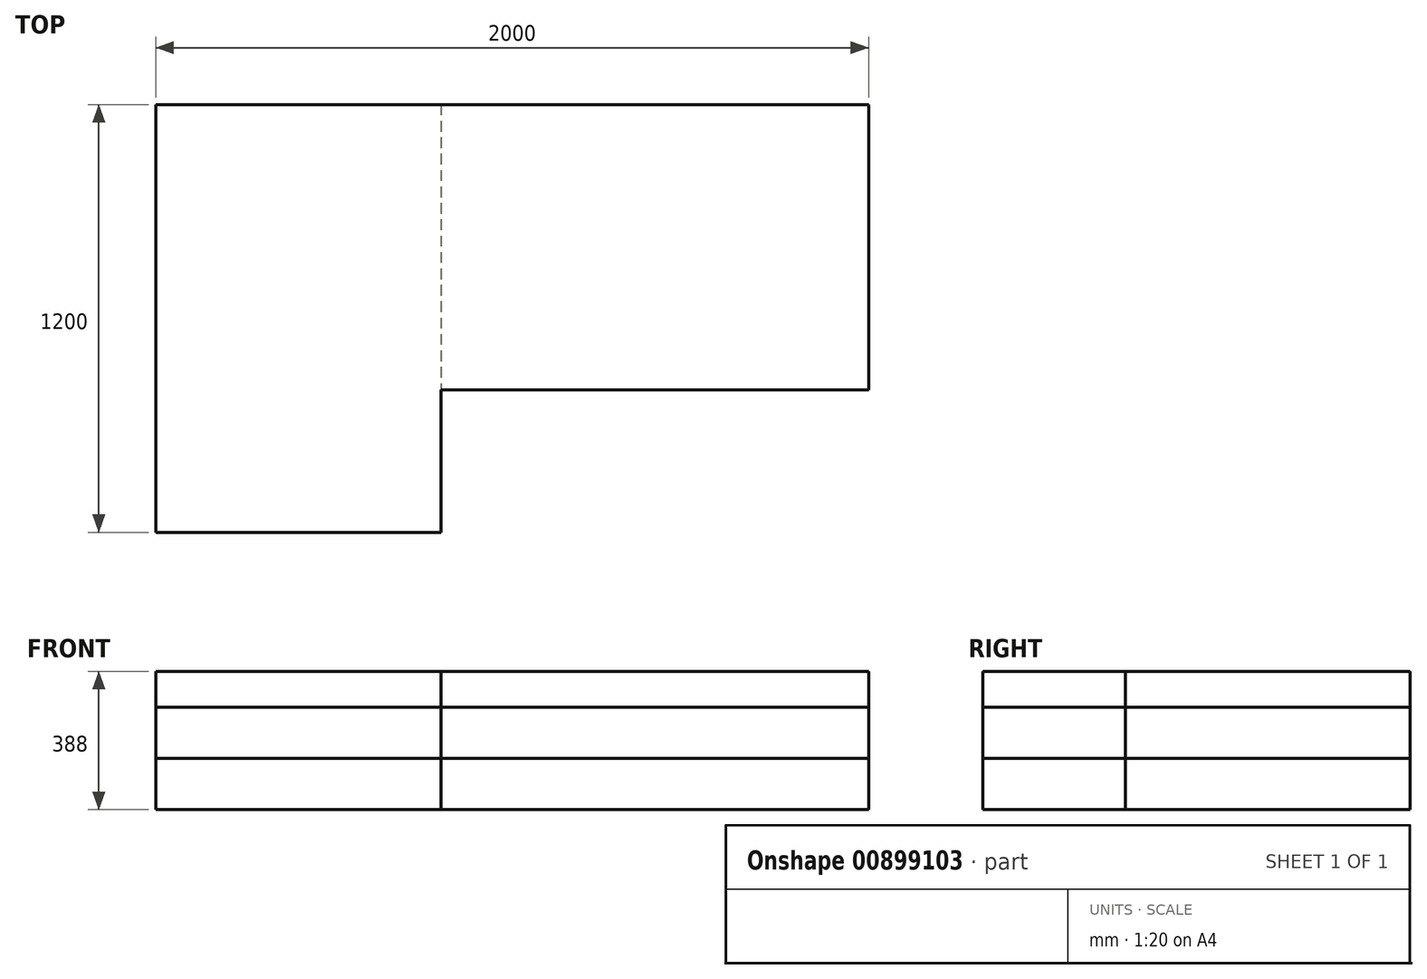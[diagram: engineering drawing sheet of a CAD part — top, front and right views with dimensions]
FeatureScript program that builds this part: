
annotation { "Feature Type Name" : "Feature", "Feature Type Description" : "" }
export const myFeature = defineFeature(function(context is Context, id is Id, definition is map)
    precondition{}
    {
        {
            var Q0;
            Q0=qCreatedBy(makeId("Top.planeOp"),FACE);
            var sketch = newSketch(context, id + "F0", { "sketchPlane" : qUnion([Q0])});
            skLineSegment(sketch, "E0.bottom", {"start": v(-200, 600) * mm, "end": v(1000, 600) * mm});
            skLineSegment(sketch, "E0.top", {"start": v(-200, -200) * mm, "end": v(1000, -200) * mm});
            skLineSegment(sketch, "E0.left", {"start": v(-200, 600) * mm, "end": v(-200, -200) * mm});
            skLineSegment(sketch, "E0.right", {"start": v(1000, 600) * mm, "end": v(1000, -200) * mm});
            skLineSegment(sketch, "E1.bottom", {"start": v(-1000, 600) * mm, "end": v(-200, 600) * mm});
            skLineSegment(sketch, "E1.top", {"start": v(-1000, -600) * mm, "end": v(-200, -600) * mm});
            skLineSegment(sketch, "E1.left", {"start": v(-1000, 600) * mm, "end": v(-1000, -600) * mm});
            skLineSegment(sketch, "E1.right", {"start": v(-200, 600) * mm, "end": v(-200, -600) * mm});
            skLineSegment(sketch, "E2", {"start": v(-1000, -600) * mm, "end": v(1000, 600) * mm, "construction": true});
            skPoint(sketch, "E3", {"position": v(0, 0) * mm});
            skSolve(sketch);
        }
        {
            var Q0;
            {var subQ1=sQuery(id+"F0.wireOp",EDGE,"E1.bottom");Q0=makeQuery(id+"F0.imprint","IMPRINT",FACE,{"disambiguationData":[TD([[makeQuery(id+"F0.imprint","IMPRINT",EDGE,{"derivedFrom":subQ1}),-1.0]])]});}
            extrude(context, id + "F1", {"entities" : qUnion([Q0]), "depth" : 144 * mm, "offsetDistance" : 25 * mm});
        }
        {
            var Q0;
            {var subQ0=sQuery(id+"F0.wireOp",EDGE,"E0.bottom");Q0=makeQuery(id+"F0.imprint","IMPRINT",FACE,{"disambiguationData":[TD([[makeQuery(id+"F0.imprint","IMPRINT",EDGE,{"derivedFrom":subQ0}),-1.0]])]});}
            extrude(context, id + "F2", {"entities" : qUnion([Q0]), "depth" : 144 * mm, "offsetDistance" : 25 * mm});
        }
        {
            var Q0;
            Q0=makeQuery(id+"F1.opExtrude","CAP_FACE",FACE,{"disambiguationData":[OSD([sQuery(id+"F0.wireOp",EDGE,"E1.bottom"),sQuery(id+"F0.wireOp",EDGE,"E1.top"),sQuery(id+"F0.wireOp",EDGE,"E1.left"),sQuery(id+"F0.wireOp",EDGE,"E1.right")])],"isStart":false});
            var sketch = newSketch(context, id + "F3", { "sketchPlane" : qUnion([Q0])});
            skLineSegment(sketch, "E4.0", {"start": v(-1000, 600) * mm, "end": v(-1000, -600) * mm});
            skLineSegment(sketch, "E5.0", {"start": v(-1000, -600) * mm, "end": v(-200, -600) * mm});
            skLineSegment(sketch, "E6.0", {"start": v(-200, 600) * mm, "end": v(-200, -600) * mm});
            skLineSegment(sketch, "E7.0", {"start": v(-1000, 600) * mm, "end": v(-200, 600) * mm});
            skLineSegment(sketch, "E8.0.0", {"start": v(1000, 600) * mm, "end": v(-200, 600) * mm});
            skLineSegment(sketch, "E8.0.1", {"start": v(-200, 600) * mm, "end": v(-200, -200) * mm});
            skLineSegment(sketch, "E8.0.2", {"start": v(-200, -200) * mm, "end": v(1000, -200) * mm});
            skLineSegment(sketch, "E8.0.3", {"start": v(1000, -200) * mm, "end": v(1000, 600) * mm});
            skSolve(sketch);
        }
        {
            var Q0;
            Q0 = qSketchRegion(id + "F3", true);
            extrude(context, id + "F4", {"entities" : qUnion([Q0]), "depth" : 144 * mm, "offsetDistance" : 25 * mm});
        }
        {
            var Q0;
            Q0=makeQuery(id+"F4.opExtrude","CAP_FACE",FACE,{"disambiguationData":[OSD([sQuery(id+"F3.wireOp",EDGE,"E4.0"),sQuery(id+"F3.wireOp",EDGE,"E5.0"),sQuery(id+"F3.wireOp",EDGE,"E6.0"),sQuery(id+"F3.wireOp",EDGE,"E7.0"),sQuery(id+"F3.wireOp",EDGE,"E8.0.0"),sQuery(id+"F3.wireOp",EDGE,"E8.0.2"),sQuery(id+"F3.wireOp",EDGE,"E8.0.3")])],"isStart":false});
            var sketch = newSketch(context, id + "F5", { "sketchPlane" : qUnion([Q0])});
            skLineSegment(sketch, "E9.0.0", {"start": v(-200, -600) * mm, "end": v(-200, -200) * mm});
            skLineSegment(sketch, "E9.0.1", {"start": v(-200, -200) * mm, "end": v(1000, -200) * mm});
            skLineSegment(sketch, "E9.0.2", {"start": v(1000, -200) * mm, "end": v(1000, 600) * mm});
            skLineSegment(sketch, "E9.0.3", {"start": v(1000, 600) * mm, "end": v(-1000, 600) * mm});
            skLineSegment(sketch, "E9.0.4", {"start": v(-1000, 600) * mm, "end": v(-1000, -600) * mm});
            skLineSegment(sketch, "E9.0.5", {"start": v(-1000, -600) * mm, "end": v(-200, -600) * mm});
            skSolve(sketch);
        }
        {
            var Q0;
            Q0 = qSketchRegion(id + "F5", true);
            extrude(context, id + "F6", {"entities" : qUnion([Q0]), "depth" : 100 * mm, "offsetDistance" : 25 * mm});
        }
    });
